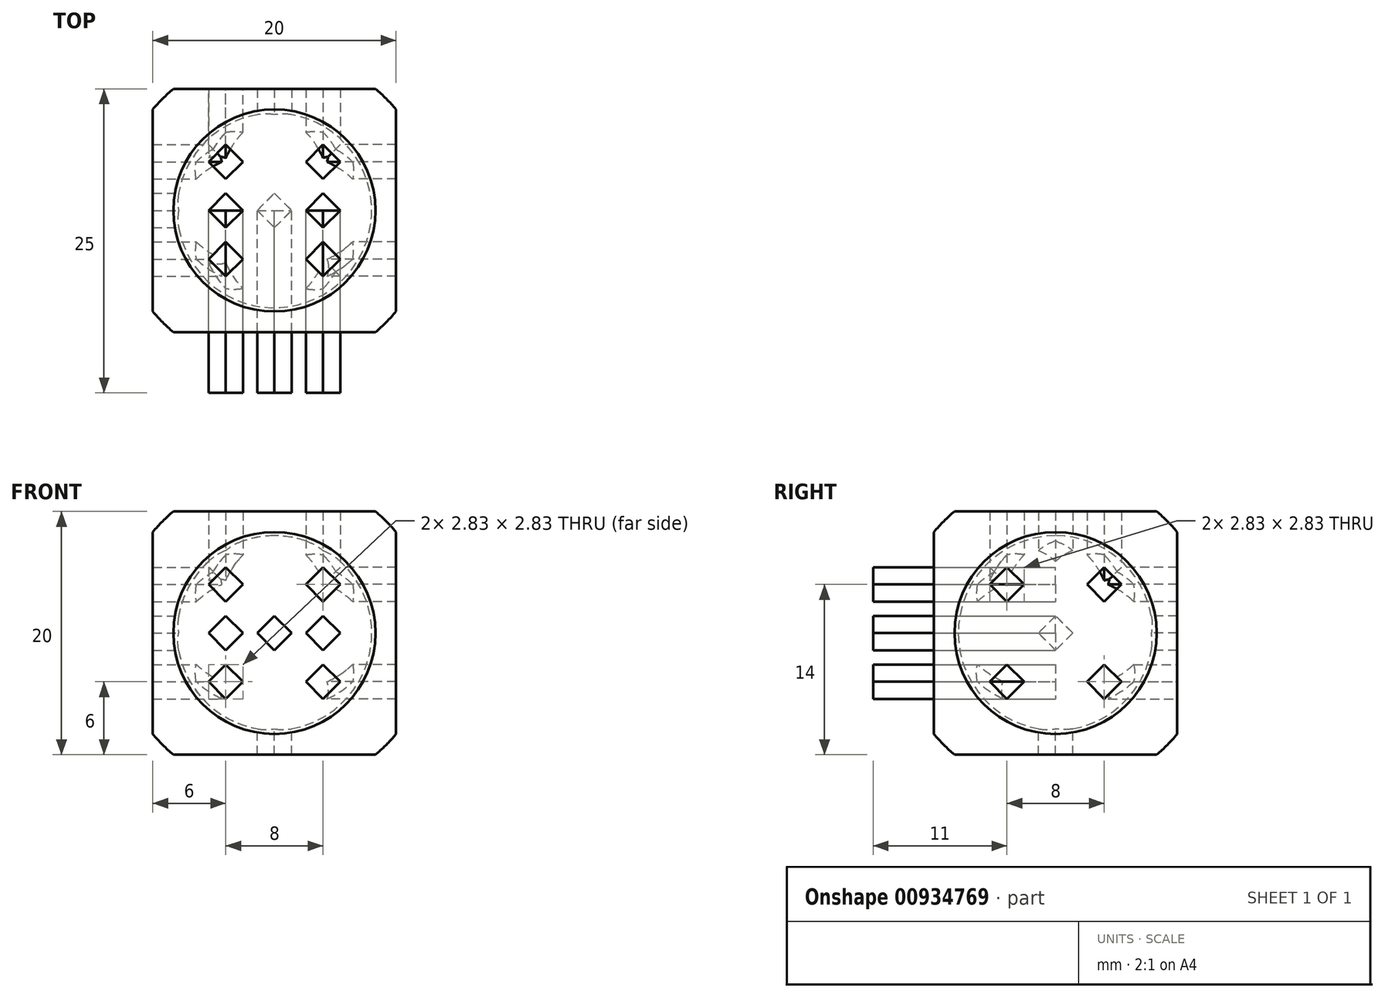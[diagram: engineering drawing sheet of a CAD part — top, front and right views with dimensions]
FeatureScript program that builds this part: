
annotation { "Feature Type Name" : "Feature", "Feature Type Description" : "" }
export const myFeature = defineFeature(function(context is Context, id is Id, definition is map)
    precondition{}
    {
        {
            var Q0;
            Q0=qCreatedBy(makeId("Front.planeOp"),FACE);
            var sketch = newSketch(context, id + "F0", { "sketchPlane" : qUnion([Q0])});
            skLineSegment(sketch, "E0.bottom", {"start": v(-10, 10) * mm, "end": v(10, 10) * mm});
            skLineSegment(sketch, "E0.top", {"start": v(-10, -10) * mm, "end": v(10, -10) * mm});
            skLineSegment(sketch, "E0.left", {"start": v(-10, 10) * mm, "end": v(-10, -10) * mm});
            skLineSegment(sketch, "E0.right", {"start": v(10, 10) * mm, "end": v(10, -10) * mm});
            skLineSegment(sketch, "E1", {"start": v(0, 0) * mm, "end": v(0, 10) * mm});
            skLineSegment(sketch, "E2", {"start": v(0, 10) * mm, "end": v(0, 0) * mm, "construction": true});
            skLineSegment(sketch, "E3", {"start": v(10, 0) * mm, "end": v(0, 0) * mm, "construction": true});
            skSolve(sketch);
        }
        {
            var Q0;
            Q0=qCreatedBy(makeId("Front.planeOp"),FACE);
            var sketch = newSketch(context, id + "F1", { "sketchPlane" : qUnion([Q0])});
            skLineSegment(sketch, "E4.bottom", {"start": v(-1, 1) * mm, "end": v(1, 1) * mm});
            skLineSegment(sketch, "E4.top", {"start": v(-1, -1) * mm, "end": v(1, -1) * mm});
            skLineSegment(sketch, "E4.left", {"start": v(-1, 1) * mm, "end": v(-1, -1) * mm});
            skLineSegment(sketch, "E4.right", {"start": v(1, 1) * mm, "end": v(1, -1) * mm});
            skSolve(sketch);
        }
        {
            var Q0;
            Q0=qCreatedBy(makeId("Right.planeOp"),FACE);
            var sketch = newSketch(context, id + "F2", { "sketchPlane" : qUnion([Q0])});
            skLineSegment(sketch, "E5", {"start": v(0, 0) * mm, "end": v(-28.1, 0) * mm, "construction": true});
            skSolve(sketch);
        }
        {
            var Q0;
            Q0 = qSketchRegion(id + "F1", true);
            extrude(context, id + "F3", {"entities" : qUnion([Q0]), "depth" : 15 * mm, "offsetDistance" : 25 * mm});
        }
        {
            var Q0;
            Q0=makeQuery(id+"F3.opExtrude","SWEPT_BODY",BODY,{"disambiguationData":[OSD([sQuery(id+"F1.wireOp",EDGE,"E4.bottom"),sQuery(id+"F1.wireOp",EDGE,"E4.top"),sQuery(id+"F1.wireOp",EDGE,"E4.left"),sQuery(id+"F1.wireOp",EDGE,"E4.right")])]});
            var Q1;
            Q1=sQuery(id+"F2.wireOp",EDGE,"E5");
            transform(context, id + "F4", {"entities" : qUnion([Q0]), "transformType" : TransformType.ROTATION, "transformAxis" : qUnion([Q1]), "angle" : 45 * degree, "makeCopy" : false});
        }
        {
            var Q0;
            Q0=makeQuery(id+"F3.opExtrude","SWEPT_BODY",BODY,{"disambiguationData":[OSD([sQuery(id+"F1.wireOp",EDGE,"E4.bottom"),sQuery(id+"F1.wireOp",EDGE,"E4.top"),sQuery(id+"F1.wireOp",EDGE,"E4.left"),sQuery(id+"F1.wireOp",EDGE,"E4.right")])]});
            transform(context, id + "F5", {"entities" : qUnion([Q0]), "transformType" : TransformType.TRANSLATION_3D, "dx" : 0 * mm, "dy" : 0 * mm, "dz" : 0 * mm, "makeCopy" : true});
        }
        {
            var Q0;
            Q0=makeQuery(id+"F5.opPattern","COPY",BODY,{"derivedFrom":makeQuery(id+"F3.opExtrude","SWEPT_BODY",BODY,{"disambiguationData":[OSD([sQuery(id+"F1.wireOp",EDGE,"E4.bottom"),sQuery(id+"F1.wireOp",EDGE,"E4.top"),sQuery(id+"F1.wireOp",EDGE,"E4.left"),sQuery(id+"F1.wireOp",EDGE,"E4.right")])]}),"instanceName":"1"});
            transform(context, id + "F6", {"entities" : qUnion([Q0]), "transformType" : TransformType.TRANSLATION_3D, "dx" : 4 * mm, "dy" : 0 * mm, "dz" : 4 * mm, "makeCopy" : false});
        }
        {
            var Q0;
            Q0=makeQuery(id+"F5.opPattern","COPY",BODY,{"derivedFrom":makeQuery(id+"F3.opExtrude","SWEPT_BODY",BODY,{"disambiguationData":[OSD([sQuery(id+"F1.wireOp",EDGE,"E4.bottom"),sQuery(id+"F1.wireOp",EDGE,"E4.top"),sQuery(id+"F1.wireOp",EDGE,"E4.left"),sQuery(id+"F1.wireOp",EDGE,"E4.right")])]}),"instanceName":"1"});
            var Q1;
            Q1=sQuery(id+"F2.wireOp",EDGE,"E5");
            transform(context, id + "F7", {"entities" : qUnion([Q0]), "transformType" : TransformType.ROTATION, "transformAxis" : qUnion([Q1]), "angle" : 90 * degree, "makeCopy" : true});
        }
        {
            var Q0;
            Q0=makeQuery(id+"F7.opPattern","COPY",BODY,{"derivedFrom":makeQuery(id+"F5.opPattern","COPY",BODY,{"derivedFrom":makeQuery(id+"F3.opExtrude","SWEPT_BODY",BODY,{"disambiguationData":[OSD([sQuery(id+"F1.wireOp",EDGE,"E4.bottom"),sQuery(id+"F1.wireOp",EDGE,"E4.top"),sQuery(id+"F1.wireOp",EDGE,"E4.left"),sQuery(id+"F1.wireOp",EDGE,"E4.right")])]}),"instanceName":"1"}),"instanceName":"1"});
            var Q1;
            Q1=makeQuery(id+"F5.opPattern","COPY",BODY,{"derivedFrom":makeQuery(id+"F3.opExtrude","SWEPT_BODY",BODY,{"disambiguationData":[OSD([sQuery(id+"F1.wireOp",EDGE,"E4.bottom"),sQuery(id+"F1.wireOp",EDGE,"E4.top"),sQuery(id+"F1.wireOp",EDGE,"E4.left"),sQuery(id+"F1.wireOp",EDGE,"E4.right")])]}),"instanceName":"1"});
            var Q2;
            Q2=qCreatedBy(makeId("Top.planeOp"),FACE);
            mirror(context, id + "F8", {"entities" : qUnion([Q0, Q1]), "mirrorPlane" : qUnion([Q2])});
        }
        {
            var Q0;
            Q0=makeQuery(id+"F3.opExtrude","SWEPT_BODY",BODY,{"disambiguationData":[OSD([sQuery(id+"F1.wireOp",EDGE,"E4.bottom"),sQuery(id+"F1.wireOp",EDGE,"E4.top"),sQuery(id+"F1.wireOp",EDGE,"E4.left"),sQuery(id+"F1.wireOp",EDGE,"E4.right")])]});
            transform(context, id + "F9", {"entities" : qUnion([Q0]), "transformType" : TransformType.TRANSLATION_3D, "dx" : 4 * mm, "dy" : 0 * mm, "dz" : 0 * mm, "makeCopy" : true});
        }
        {
            var Q0;
            Q0=makeQuery(id+"F9.opPattern","COPY",BODY,{"derivedFrom":makeQuery(id+"F3.opExtrude","SWEPT_BODY",BODY,{"disambiguationData":[OSD([sQuery(id+"F1.wireOp",EDGE,"E4.bottom"),sQuery(id+"F1.wireOp",EDGE,"E4.top"),sQuery(id+"F1.wireOp",EDGE,"E4.left"),sQuery(id+"F1.wireOp",EDGE,"E4.right")])]}),"instanceName":"1"});
            var Q1;
            Q1=sQuery(id+"F2.wireOp",EDGE,"E5");
            transform(context, id + "F10", {"entities" : qUnion([Q0]), "transformType" : TransformType.ROTATION, "transformAxis" : qUnion([Q1]), "angle" : 180 * degree, "makeCopy" : true});
        }
        {
            var Q0;
            Q0=makeQuery(id+"F3.opExtrude","SWEPT_BODY",BODY,{"disambiguationData":[OSD([sQuery(id+"F1.wireOp",EDGE,"E4.bottom"),sQuery(id+"F1.wireOp",EDGE,"E4.top"),sQuery(id+"F1.wireOp",EDGE,"E4.left"),sQuery(id+"F1.wireOp",EDGE,"E4.right")])]});
            var Q1;
            Q1=sQuery(id+"F0.wireOp",EDGE,"E3");
            transform(context, id + "F11", {"entities" : qUnion([Q0]), "transformType" : TransformType.ROTATION, "transformAxis" : qUnion([Q1]), "angle" : 90 * degree, "oppositeDirection" : true, "makeCopy" : true});
        }
        {
            var Q0;
            Q0=makeQuery(id+"F7.opPattern","COPY",BODY,{"derivedFrom":makeQuery(id+"F5.opPattern","COPY",BODY,{"derivedFrom":makeQuery(id+"F3.opExtrude","SWEPT_BODY",BODY,{"disambiguationData":[OSD([sQuery(id+"F1.wireOp",EDGE,"E4.bottom"),sQuery(id+"F1.wireOp",EDGE,"E4.top"),sQuery(id+"F1.wireOp",EDGE,"E4.left"),sQuery(id+"F1.wireOp",EDGE,"E4.right")])]}),"instanceName":"1"}),"instanceName":"1"});
            var Q1;
            Q1=makeQuery(id+"F10.opPattern","COPY",BODY,{"derivedFrom":makeQuery(id+"F9.opPattern","COPY",BODY,{"derivedFrom":makeQuery(id+"F3.opExtrude","SWEPT_BODY",BODY,{"disambiguationData":[OSD([sQuery(id+"F1.wireOp",EDGE,"E4.bottom"),sQuery(id+"F1.wireOp",EDGE,"E4.top"),sQuery(id+"F1.wireOp",EDGE,"E4.left"),sQuery(id+"F1.wireOp",EDGE,"E4.right")])]}),"instanceName":"1"}),"instanceName":"1"});
            var Q2;
            Q2=makeQuery(id+"F8.opPattern","COPY",BODY,{"derivedFrom":makeQuery(id+"F7.opPattern","COPY",BODY,{"derivedFrom":makeQuery(id+"F5.opPattern","COPY",BODY,{"derivedFrom":makeQuery(id+"F3.opExtrude","SWEPT_BODY",BODY,{"disambiguationData":[OSD([sQuery(id+"F1.wireOp",EDGE,"E4.bottom"),sQuery(id+"F1.wireOp",EDGE,"E4.top"),sQuery(id+"F1.wireOp",EDGE,"E4.left"),sQuery(id+"F1.wireOp",EDGE,"E4.right")])]}),"instanceName":"1"}),"instanceName":"1"}),"instanceName":"1"});
            var Q3;
            Q3=makeQuery(id+"F5.opPattern","COPY",BODY,{"derivedFrom":makeQuery(id+"F3.opExtrude","SWEPT_BODY",BODY,{"disambiguationData":[OSD([sQuery(id+"F1.wireOp",EDGE,"E4.bottom"),sQuery(id+"F1.wireOp",EDGE,"E4.top"),sQuery(id+"F1.wireOp",EDGE,"E4.left"),sQuery(id+"F1.wireOp",EDGE,"E4.right")])]}),"instanceName":"1"});
            var Q4;
            Q4=makeQuery(id+"F9.opPattern","COPY",BODY,{"derivedFrom":makeQuery(id+"F3.opExtrude","SWEPT_BODY",BODY,{"disambiguationData":[OSD([sQuery(id+"F1.wireOp",EDGE,"E4.bottom"),sQuery(id+"F1.wireOp",EDGE,"E4.top"),sQuery(id+"F1.wireOp",EDGE,"E4.left"),sQuery(id+"F1.wireOp",EDGE,"E4.right")])]}),"instanceName":"1"});
            var Q5;
            Q5=makeQuery(id+"F8.opPattern","COPY",BODY,{"derivedFrom":makeQuery(id+"F5.opPattern","COPY",BODY,{"derivedFrom":makeQuery(id+"F3.opExtrude","SWEPT_BODY",BODY,{"disambiguationData":[OSD([sQuery(id+"F1.wireOp",EDGE,"E4.bottom"),sQuery(id+"F1.wireOp",EDGE,"E4.top"),sQuery(id+"F1.wireOp",EDGE,"E4.left"),sQuery(id+"F1.wireOp",EDGE,"E4.right")])]}),"instanceName":"1"}),"instanceName":"1"});
            var Q6;
            Q6=sQuery(id+"F0.wireOp",EDGE,"E3");
            transform(context, id + "F12", {"entities" : qUnion([Q0, Q1, Q2, Q3, Q4, Q5]), "transformType" : TransformType.ROTATION, "transformAxis" : qUnion([Q6]), "angle" : 90 * degree, "makeCopy" : true});
        }
        {
            var Q0;
            Q0=makeQuery(id+"F7.opPattern","COPY",BODY,{"derivedFrom":makeQuery(id+"F5.opPattern","COPY",BODY,{"derivedFrom":makeQuery(id+"F3.opExtrude","SWEPT_BODY",BODY,{"disambiguationData":[OSD([sQuery(id+"F1.wireOp",EDGE,"E4.bottom"),sQuery(id+"F1.wireOp",EDGE,"E4.top"),sQuery(id+"F1.wireOp",EDGE,"E4.left"),sQuery(id+"F1.wireOp",EDGE,"E4.right")])]}),"instanceName":"1"}),"instanceName":"1"});
            var Q1;
            Q1=makeQuery(id+"F8.opPattern","COPY",BODY,{"derivedFrom":makeQuery(id+"F7.opPattern","COPY",BODY,{"derivedFrom":makeQuery(id+"F5.opPattern","COPY",BODY,{"derivedFrom":makeQuery(id+"F3.opExtrude","SWEPT_BODY",BODY,{"disambiguationData":[OSD([sQuery(id+"F1.wireOp",EDGE,"E4.bottom"),sQuery(id+"F1.wireOp",EDGE,"E4.top"),sQuery(id+"F1.wireOp",EDGE,"E4.left"),sQuery(id+"F1.wireOp",EDGE,"E4.right")])]}),"instanceName":"1"}),"instanceName":"1"}),"instanceName":"1"});
            var Q2;
            Q2=makeQuery(id+"F8.opPattern","COPY",BODY,{"derivedFrom":makeQuery(id+"F5.opPattern","COPY",BODY,{"derivedFrom":makeQuery(id+"F3.opExtrude","SWEPT_BODY",BODY,{"disambiguationData":[OSD([sQuery(id+"F1.wireOp",EDGE,"E4.bottom"),sQuery(id+"F1.wireOp",EDGE,"E4.top"),sQuery(id+"F1.wireOp",EDGE,"E4.left"),sQuery(id+"F1.wireOp",EDGE,"E4.right")])]}),"instanceName":"1"}),"instanceName":"1"});
            var Q3;
            Q3=makeQuery(id+"F5.opPattern","COPY",BODY,{"derivedFrom":makeQuery(id+"F3.opExtrude","SWEPT_BODY",BODY,{"disambiguationData":[OSD([sQuery(id+"F1.wireOp",EDGE,"E4.bottom"),sQuery(id+"F1.wireOp",EDGE,"E4.top"),sQuery(id+"F1.wireOp",EDGE,"E4.left"),sQuery(id+"F1.wireOp",EDGE,"E4.right")])]}),"instanceName":"1"});
            var Q4;
            Q4=makeQuery(id+"F3.opExtrude","SWEPT_BODY",BODY,{"disambiguationData":[OSD([sQuery(id+"F1.wireOp",EDGE,"E4.bottom"),sQuery(id+"F1.wireOp",EDGE,"E4.top"),sQuery(id+"F1.wireOp",EDGE,"E4.left"),sQuery(id+"F1.wireOp",EDGE,"E4.right")])]});
            var Q5;
            Q5=sQuery(id+"F0.wireOp",EDGE,"E1");
            transform(context, id + "F13", {"entities" : qUnion([Q0, Q1, Q2, Q3, Q4]), "transformType" : TransformType.ROTATION, "transformAxis" : qUnion([Q5]), "angle" : 180 * degree, "makeCopy" : true});
        }
        {
            var Q0;
            Q0=makeQuery(id+"F7.opPattern","COPY",BODY,{"derivedFrom":makeQuery(id+"F5.opPattern","COPY",BODY,{"derivedFrom":makeQuery(id+"F3.opExtrude","SWEPT_BODY",BODY,{"disambiguationData":[OSD([sQuery(id+"F1.wireOp",EDGE,"E4.bottom"),sQuery(id+"F1.wireOp",EDGE,"E4.top"),sQuery(id+"F1.wireOp",EDGE,"E4.left"),sQuery(id+"F1.wireOp",EDGE,"E4.right")])]}),"instanceName":"1"}),"instanceName":"1"});
            var Q1;
            Q1=makeQuery(id+"F8.opPattern","COPY",BODY,{"derivedFrom":makeQuery(id+"F5.opPattern","COPY",BODY,{"derivedFrom":makeQuery(id+"F3.opExtrude","SWEPT_BODY",BODY,{"disambiguationData":[OSD([sQuery(id+"F1.wireOp",EDGE,"E4.bottom"),sQuery(id+"F1.wireOp",EDGE,"E4.top"),sQuery(id+"F1.wireOp",EDGE,"E4.left"),sQuery(id+"F1.wireOp",EDGE,"E4.right")])]}),"instanceName":"1"}),"instanceName":"1"});
            var Q2;
            Q2=makeQuery(id+"F5.opPattern","COPY",BODY,{"derivedFrom":makeQuery(id+"F3.opExtrude","SWEPT_BODY",BODY,{"disambiguationData":[OSD([sQuery(id+"F1.wireOp",EDGE,"E4.bottom"),sQuery(id+"F1.wireOp",EDGE,"E4.top"),sQuery(id+"F1.wireOp",EDGE,"E4.left"),sQuery(id+"F1.wireOp",EDGE,"E4.right")])]}),"instanceName":"1"});
            var Q3;
            Q3=makeQuery(id+"F8.opPattern","COPY",BODY,{"derivedFrom":makeQuery(id+"F7.opPattern","COPY",BODY,{"derivedFrom":makeQuery(id+"F5.opPattern","COPY",BODY,{"derivedFrom":makeQuery(id+"F3.opExtrude","SWEPT_BODY",BODY,{"disambiguationData":[OSD([sQuery(id+"F1.wireOp",EDGE,"E4.bottom"),sQuery(id+"F1.wireOp",EDGE,"E4.top"),sQuery(id+"F1.wireOp",EDGE,"E4.left"),sQuery(id+"F1.wireOp",EDGE,"E4.right")])]}),"instanceName":"1"}),"instanceName":"1"}),"instanceName":"1"});
            var Q4;
            Q4=sQuery(id+"F0.wireOp",EDGE,"E2");
            transform(context, id + "F14", {"entities" : qUnion([Q0, Q1, Q2, Q3]), "transformType" : TransformType.ROTATION, "transformAxis" : qUnion([Q4]), "angle" : 90 * degree, "oppositeDirection" : true, "makeCopy" : true});
        }
        {
            var Q0;
            Q0=makeQuery(id+"F8.opPattern","COPY",BODY,{"derivedFrom":makeQuery(id+"F7.opPattern","COPY",BODY,{"derivedFrom":makeQuery(id+"F5.opPattern","COPY",BODY,{"derivedFrom":makeQuery(id+"F3.opExtrude","SWEPT_BODY",BODY,{"disambiguationData":[OSD([sQuery(id+"F1.wireOp",EDGE,"E4.bottom"),sQuery(id+"F1.wireOp",EDGE,"E4.top"),sQuery(id+"F1.wireOp",EDGE,"E4.left"),sQuery(id+"F1.wireOp",EDGE,"E4.right")])]}),"instanceName":"1"}),"instanceName":"1"}),"instanceName":"1"});
            var Q1;
            Q1=makeQuery(id+"F3.opExtrude","SWEPT_BODY",BODY,{"disambiguationData":[OSD([sQuery(id+"F1.wireOp",EDGE,"E4.bottom"),sQuery(id+"F1.wireOp",EDGE,"E4.top"),sQuery(id+"F1.wireOp",EDGE,"E4.left"),sQuery(id+"F1.wireOp",EDGE,"E4.right")])]});
            var Q2;
            Q2=makeQuery(id+"F5.opPattern","COPY",BODY,{"derivedFrom":makeQuery(id+"F3.opExtrude","SWEPT_BODY",BODY,{"disambiguationData":[OSD([sQuery(id+"F1.wireOp",EDGE,"E4.bottom"),sQuery(id+"F1.wireOp",EDGE,"E4.top"),sQuery(id+"F1.wireOp",EDGE,"E4.left"),sQuery(id+"F1.wireOp",EDGE,"E4.right")])]}),"instanceName":"1"});
            var Q3;
            Q3=sQuery(id+"F0.wireOp",EDGE,"E2");
            transform(context, id + "F15", {"entities" : qUnion([Q0, Q1, Q2]), "transformType" : TransformType.ROTATION, "transformAxis" : qUnion([Q3]), "angle" : 90 * degree, "makeCopy" : true});
        }
        {
            var Q0;
            Q0=makeQuery(id+"F8.opPattern","COPY",BODY,{"derivedFrom":makeQuery(id+"F7.opPattern","COPY",BODY,{"derivedFrom":makeQuery(id+"F5.opPattern","COPY",BODY,{"derivedFrom":makeQuery(id+"F3.opExtrude","SWEPT_BODY",BODY,{"disambiguationData":[OSD([sQuery(id+"F1.wireOp",EDGE,"E4.bottom"),sQuery(id+"F1.wireOp",EDGE,"E4.top"),sQuery(id+"F1.wireOp",EDGE,"E4.left"),sQuery(id+"F1.wireOp",EDGE,"E4.right")])]}),"instanceName":"1"}),"instanceName":"1"}),"instanceName":"1"});
            var Q1;
            Q1=makeQuery(id+"F5.opPattern","COPY",BODY,{"derivedFrom":makeQuery(id+"F3.opExtrude","SWEPT_BODY",BODY,{"disambiguationData":[OSD([sQuery(id+"F1.wireOp",EDGE,"E4.bottom"),sQuery(id+"F1.wireOp",EDGE,"E4.top"),sQuery(id+"F1.wireOp",EDGE,"E4.left"),sQuery(id+"F1.wireOp",EDGE,"E4.right")])]}),"instanceName":"1"});
            transform(context, id + "F16", {"entities" : qUnion([Q0, Q1]), "transformType" : TransformType.TRANSLATION_3D, "dx" : 0 * mm, "dy" : 0 * mm, "dz" : 0 * mm, "makeCopy" : true});
        }
        {
            var Q0;
            Q0=qCreatedBy(makeId("Front.planeOp"),FACE);
            var sketch = newSketch(context, id + "F17", { "sketchPlane" : qUnion([Q0])});
            skArc(sketch, "E6", {"start": v(0, -13) * mm, "mid": v(13, 0) * mm, "end": v(0, 13) * mm});
            skArc(sketch, "E7", {"start": v(0, -8) * mm, "mid": v(8, 0) * mm, "end": v(0, 8) * mm});
            skLineSegment(sketch, "E8", {"start": v(0, 13) * mm, "end": v(0, 8) * mm});
            skLineSegment(sketch, "E9", {"start": v(0, -8) * mm, "end": v(0, -13) * mm});
            skSolve(sketch);
        }
        {
            var Q0;
            Q0 = qSketchRegion(id + "F0", true);
            extrude(context, id + "F18", {"entities" : qUnion([Q0]), "endBound" : BoundingType.SYMMETRIC, "depth" : 20 * mm, "offsetDistance" : 25 * mm});
        }
        {
            var Q0;
            Q0 = qSketchRegion(id + "F17", true);
            var Q1;
            Q1=sQuery(id+"F0.wireOp",EDGE,"E1");
            revolve(context, id + "F19", {"surfaceOperationType" : NewSurfaceOperationType.NEW, "entities" : qUnion([Q0]), "axis" : qUnion([Q1]), "revolveType" : RevolveType.FULL});
        }
        {
            var Q0;
            Q0=makeQuery(id+"F18.opExtrude","SWEPT_BODY",BODY,{"disambiguationData":[OSD([sQuery(id+"F0.wireOp",EDGE,"E0.bottom"),sQuery(id+"F0.wireOp",EDGE,"E0.top"),sQuery(id+"F0.wireOp",EDGE,"E0.left"),sQuery(id+"F0.wireOp",EDGE,"E0.right")])]});
            var Q1;
            Q1=makeQuery(id+"F19.opRevolve","SWEPT_BODY",BODY,{"disambiguationData":[OSD([sQuery(id+"F17.wireOp",EDGE,"E6"),sQuery(id+"F17.wireOp",EDGE,"E7"),sQuery(id+"F17.wireOp",EDGE,"E8"),sQuery(id+"F17.wireOp",EDGE,"E9")])]});
            booleanBodies(context, id + "F20", {"operationType" : BooleanOperationType.INTERSECTION, "tools" : qUnion([Q0, Q1])});
        }
        {
            var Q0;
            Q0=makeQuery(id+"F16.opPattern","COPY",BODY,{"derivedFrom":makeQuery(id+"F5.opPattern","COPY",BODY,{"derivedFrom":makeQuery(id+"F3.opExtrude","SWEPT_BODY",BODY,{"disambiguationData":[OSD([sQuery(id+"F1.wireOp",EDGE,"E4.bottom"),sQuery(id+"F1.wireOp",EDGE,"E4.top"),sQuery(id+"F1.wireOp",EDGE,"E4.left"),sQuery(id+"F1.wireOp",EDGE,"E4.right")])]}),"instanceName":"1"}),"instanceName":"1"});
            var Q1;
            Q1=makeQuery(id+"F16.opPattern","COPY",BODY,{"derivedFrom":makeQuery(id+"F8.opPattern","COPY",BODY,{"derivedFrom":makeQuery(id+"F7.opPattern","COPY",BODY,{"derivedFrom":makeQuery(id+"F5.opPattern","COPY",BODY,{"derivedFrom":makeQuery(id+"F3.opExtrude","SWEPT_BODY",BODY,{"disambiguationData":[OSD([sQuery(id+"F1.wireOp",EDGE,"E4.bottom"),sQuery(id+"F1.wireOp",EDGE,"E4.top"),sQuery(id+"F1.wireOp",EDGE,"E4.left"),sQuery(id+"F1.wireOp",EDGE,"E4.right")])]}),"instanceName":"1"}),"instanceName":"1"}),"instanceName":"1"}),"instanceName":"1"});
            var Q2;
            Q2=makeQuery(id+"F14.opPattern","COPY",BODY,{"derivedFrom":makeQuery(id+"F8.opPattern","COPY",BODY,{"derivedFrom":makeQuery(id+"F7.opPattern","COPY",BODY,{"derivedFrom":makeQuery(id+"F5.opPattern","COPY",BODY,{"derivedFrom":makeQuery(id+"F3.opExtrude","SWEPT_BODY",BODY,{"disambiguationData":[OSD([sQuery(id+"F1.wireOp",EDGE,"E4.bottom"),sQuery(id+"F1.wireOp",EDGE,"E4.top"),sQuery(id+"F1.wireOp",EDGE,"E4.left"),sQuery(id+"F1.wireOp",EDGE,"E4.right")])]}),"instanceName":"1"}),"instanceName":"1"}),"instanceName":"1"}),"instanceName":"1"});
            var Q3;
            Q3=makeQuery(id+"F14.opPattern","COPY",BODY,{"derivedFrom":makeQuery(id+"F7.opPattern","COPY",BODY,{"derivedFrom":makeQuery(id+"F5.opPattern","COPY",BODY,{"derivedFrom":makeQuery(id+"F3.opExtrude","SWEPT_BODY",BODY,{"disambiguationData":[OSD([sQuery(id+"F1.wireOp",EDGE,"E4.bottom"),sQuery(id+"F1.wireOp",EDGE,"E4.top"),sQuery(id+"F1.wireOp",EDGE,"E4.left"),sQuery(id+"F1.wireOp",EDGE,"E4.right")])]}),"instanceName":"1"}),"instanceName":"1"}),"instanceName":"1"});
            var Q4;
            Q4=makeQuery(id+"F14.opPattern","COPY",BODY,{"derivedFrom":makeQuery(id+"F5.opPattern","COPY",BODY,{"derivedFrom":makeQuery(id+"F3.opExtrude","SWEPT_BODY",BODY,{"disambiguationData":[OSD([sQuery(id+"F1.wireOp",EDGE,"E4.bottom"),sQuery(id+"F1.wireOp",EDGE,"E4.top"),sQuery(id+"F1.wireOp",EDGE,"E4.left"),sQuery(id+"F1.wireOp",EDGE,"E4.right")])]}),"instanceName":"1"}),"instanceName":"1"});
            var Q5;
            Q5=makeQuery(id+"F14.opPattern","COPY",BODY,{"derivedFrom":makeQuery(id+"F8.opPattern","COPY",BODY,{"derivedFrom":makeQuery(id+"F5.opPattern","COPY",BODY,{"derivedFrom":makeQuery(id+"F3.opExtrude","SWEPT_BODY",BODY,{"disambiguationData":[OSD([sQuery(id+"F1.wireOp",EDGE,"E4.bottom"),sQuery(id+"F1.wireOp",EDGE,"E4.top"),sQuery(id+"F1.wireOp",EDGE,"E4.left"),sQuery(id+"F1.wireOp",EDGE,"E4.right")])]}),"instanceName":"1"}),"instanceName":"1"}),"instanceName":"1"});
            var Q6;
            Q6=makeQuery(id+"F12.opPattern","COPY",BODY,{"derivedFrom":makeQuery(id+"F8.opPattern","COPY",BODY,{"derivedFrom":makeQuery(id+"F5.opPattern","COPY",BODY,{"derivedFrom":makeQuery(id+"F3.opExtrude","SWEPT_BODY",BODY,{"disambiguationData":[OSD([sQuery(id+"F1.wireOp",EDGE,"E4.bottom"),sQuery(id+"F1.wireOp",EDGE,"E4.top"),sQuery(id+"F1.wireOp",EDGE,"E4.left"),sQuery(id+"F1.wireOp",EDGE,"E4.right")])]}),"instanceName":"1"}),"instanceName":"1"}),"instanceName":"1"});
            var Q7;
            Q7=makeQuery(id+"F12.opPattern","COPY",BODY,{"derivedFrom":makeQuery(id+"F9.opPattern","COPY",BODY,{"derivedFrom":makeQuery(id+"F3.opExtrude","SWEPT_BODY",BODY,{"disambiguationData":[OSD([sQuery(id+"F1.wireOp",EDGE,"E4.bottom"),sQuery(id+"F1.wireOp",EDGE,"E4.top"),sQuery(id+"F1.wireOp",EDGE,"E4.left"),sQuery(id+"F1.wireOp",EDGE,"E4.right")])]}),"instanceName":"1"}),"instanceName":"1"});
            var Q8;
            Q8=makeQuery(id+"F13.opPattern","COPY",BODY,{"derivedFrom":makeQuery(id+"F5.opPattern","COPY",BODY,{"derivedFrom":makeQuery(id+"F3.opExtrude","SWEPT_BODY",BODY,{"disambiguationData":[OSD([sQuery(id+"F1.wireOp",EDGE,"E4.bottom"),sQuery(id+"F1.wireOp",EDGE,"E4.top"),sQuery(id+"F1.wireOp",EDGE,"E4.left"),sQuery(id+"F1.wireOp",EDGE,"E4.right")])]}),"instanceName":"1"}),"instanceName":"1"});
            var Q9;
            Q9=makeQuery(id+"F12.opPattern","COPY",BODY,{"derivedFrom":makeQuery(id+"F5.opPattern","COPY",BODY,{"derivedFrom":makeQuery(id+"F3.opExtrude","SWEPT_BODY",BODY,{"disambiguationData":[OSD([sQuery(id+"F1.wireOp",EDGE,"E4.bottom"),sQuery(id+"F1.wireOp",EDGE,"E4.top"),sQuery(id+"F1.wireOp",EDGE,"E4.left"),sQuery(id+"F1.wireOp",EDGE,"E4.right")])]}),"instanceName":"1"}),"instanceName":"1"});
            var Q10;
            Q10=makeQuery(id+"F12.opPattern","COPY",BODY,{"derivedFrom":makeQuery(id+"F7.opPattern","COPY",BODY,{"derivedFrom":makeQuery(id+"F5.opPattern","COPY",BODY,{"derivedFrom":makeQuery(id+"F3.opExtrude","SWEPT_BODY",BODY,{"disambiguationData":[OSD([sQuery(id+"F1.wireOp",EDGE,"E4.bottom"),sQuery(id+"F1.wireOp",EDGE,"E4.top"),sQuery(id+"F1.wireOp",EDGE,"E4.left"),sQuery(id+"F1.wireOp",EDGE,"E4.right")])]}),"instanceName":"1"}),"instanceName":"1"}),"instanceName":"1"});
            var Q11;
            Q11=makeQuery(id+"F12.opPattern","COPY",BODY,{"derivedFrom":makeQuery(id+"F10.opPattern","COPY",BODY,{"derivedFrom":makeQuery(id+"F9.opPattern","COPY",BODY,{"derivedFrom":makeQuery(id+"F3.opExtrude","SWEPT_BODY",BODY,{"disambiguationData":[OSD([sQuery(id+"F1.wireOp",EDGE,"E4.bottom"),sQuery(id+"F1.wireOp",EDGE,"E4.top"),sQuery(id+"F1.wireOp",EDGE,"E4.left"),sQuery(id+"F1.wireOp",EDGE,"E4.right")])]}),"instanceName":"1"}),"instanceName":"1"}),"instanceName":"1"});
            var Q12;
            Q12=makeQuery(id+"F12.opPattern","COPY",BODY,{"derivedFrom":makeQuery(id+"F8.opPattern","COPY",BODY,{"derivedFrom":makeQuery(id+"F7.opPattern","COPY",BODY,{"derivedFrom":makeQuery(id+"F5.opPattern","COPY",BODY,{"derivedFrom":makeQuery(id+"F3.opExtrude","SWEPT_BODY",BODY,{"disambiguationData":[OSD([sQuery(id+"F1.wireOp",EDGE,"E4.bottom"),sQuery(id+"F1.wireOp",EDGE,"E4.top"),sQuery(id+"F1.wireOp",EDGE,"E4.left"),sQuery(id+"F1.wireOp",EDGE,"E4.right")])]}),"instanceName":"1"}),"instanceName":"1"}),"instanceName":"1"}),"instanceName":"1"});
            var Q13;
            Q13=makeQuery(id+"F13.opPattern","COPY",BODY,{"derivedFrom":makeQuery(id+"F7.opPattern","COPY",BODY,{"derivedFrom":makeQuery(id+"F5.opPattern","COPY",BODY,{"derivedFrom":makeQuery(id+"F3.opExtrude","SWEPT_BODY",BODY,{"disambiguationData":[OSD([sQuery(id+"F1.wireOp",EDGE,"E4.bottom"),sQuery(id+"F1.wireOp",EDGE,"E4.top"),sQuery(id+"F1.wireOp",EDGE,"E4.left"),sQuery(id+"F1.wireOp",EDGE,"E4.right")])]}),"instanceName":"1"}),"instanceName":"1"}),"instanceName":"1"});
            var Q14;
            Q14=makeQuery(id+"F13.opPattern","COPY",BODY,{"derivedFrom":makeQuery(id+"F8.opPattern","COPY",BODY,{"derivedFrom":makeQuery(id+"F7.opPattern","COPY",BODY,{"derivedFrom":makeQuery(id+"F5.opPattern","COPY",BODY,{"derivedFrom":makeQuery(id+"F3.opExtrude","SWEPT_BODY",BODY,{"disambiguationData":[OSD([sQuery(id+"F1.wireOp",EDGE,"E4.bottom"),sQuery(id+"F1.wireOp",EDGE,"E4.top"),sQuery(id+"F1.wireOp",EDGE,"E4.left"),sQuery(id+"F1.wireOp",EDGE,"E4.right")])]}),"instanceName":"1"}),"instanceName":"1"}),"instanceName":"1"}),"instanceName":"1"});
            var Q15;
            Q15=makeQuery(id+"F13.opPattern","COPY",BODY,{"derivedFrom":makeQuery(id+"F8.opPattern","COPY",BODY,{"derivedFrom":makeQuery(id+"F5.opPattern","COPY",BODY,{"derivedFrom":makeQuery(id+"F3.opExtrude","SWEPT_BODY",BODY,{"disambiguationData":[OSD([sQuery(id+"F1.wireOp",EDGE,"E4.bottom"),sQuery(id+"F1.wireOp",EDGE,"E4.top"),sQuery(id+"F1.wireOp",EDGE,"E4.left"),sQuery(id+"F1.wireOp",EDGE,"E4.right")])]}),"instanceName":"1"}),"instanceName":"1"}),"instanceName":"1"});
            var Q16;
            Q16=makeQuery(id+"F13.opPattern","COPY",BODY,{"derivedFrom":makeQuery(id+"F3.opExtrude","SWEPT_BODY",BODY,{"disambiguationData":[OSD([sQuery(id+"F1.wireOp",EDGE,"E4.bottom"),sQuery(id+"F1.wireOp",EDGE,"E4.top"),sQuery(id+"F1.wireOp",EDGE,"E4.left"),sQuery(id+"F1.wireOp",EDGE,"E4.right")])]}),"instanceName":"1"});
            var Q17;
            Q17=makeQuery(id+"F11.opPattern","COPY",BODY,{"derivedFrom":makeQuery(id+"F3.opExtrude","SWEPT_BODY",BODY,{"disambiguationData":[OSD([sQuery(id+"F1.wireOp",EDGE,"E4.bottom"),sQuery(id+"F1.wireOp",EDGE,"E4.top"),sQuery(id+"F1.wireOp",EDGE,"E4.left"),sQuery(id+"F1.wireOp",EDGE,"E4.right")])]}),"instanceName":"1"});
            var Q18;
            Q18=makeQuery(id+"F15.opPattern","COPY",BODY,{"derivedFrom":makeQuery(id+"F3.opExtrude","SWEPT_BODY",BODY,{"disambiguationData":[OSD([sQuery(id+"F1.wireOp",EDGE,"E4.bottom"),sQuery(id+"F1.wireOp",EDGE,"E4.top"),sQuery(id+"F1.wireOp",EDGE,"E4.left"),sQuery(id+"F1.wireOp",EDGE,"E4.right")])]}),"instanceName":"1"});
            var Q19;
            Q19=makeQuery(id+"F15.opPattern","COPY",BODY,{"derivedFrom":makeQuery(id+"F8.opPattern","COPY",BODY,{"derivedFrom":makeQuery(id+"F7.opPattern","COPY",BODY,{"derivedFrom":makeQuery(id+"F5.opPattern","COPY",BODY,{"derivedFrom":makeQuery(id+"F3.opExtrude","SWEPT_BODY",BODY,{"disambiguationData":[OSD([sQuery(id+"F1.wireOp",EDGE,"E4.bottom"),sQuery(id+"F1.wireOp",EDGE,"E4.top"),sQuery(id+"F1.wireOp",EDGE,"E4.left"),sQuery(id+"F1.wireOp",EDGE,"E4.right")])]}),"instanceName":"1"}),"instanceName":"1"}),"instanceName":"1"}),"instanceName":"1"});
            var Q20;
            Q20=makeQuery(id+"F15.opPattern","COPY",BODY,{"derivedFrom":makeQuery(id+"F5.opPattern","COPY",BODY,{"derivedFrom":makeQuery(id+"F3.opExtrude","SWEPT_BODY",BODY,{"disambiguationData":[OSD([sQuery(id+"F1.wireOp",EDGE,"E4.bottom"),sQuery(id+"F1.wireOp",EDGE,"E4.top"),sQuery(id+"F1.wireOp",EDGE,"E4.left"),sQuery(id+"F1.wireOp",EDGE,"E4.right")])]}),"instanceName":"1"}),"instanceName":"1"});
            var Q21;
            Q21=makeQuery(id+"F20.opBoolean","INTERSECT",BODY,{"derivedFrom":[makeQuery(id+"F18.opExtrude","SWEPT_BODY",BODY,{"disambiguationData":[OSD([sQuery(id+"F0.wireOp",EDGE,"E0.bottom"),sQuery(id+"F0.wireOp",EDGE,"E0.top"),sQuery(id+"F0.wireOp",EDGE,"E0.left"),sQuery(id+"F0.wireOp",EDGE,"E0.right")])]}),makeQuery(id+"F19.opRevolve","SWEPT_BODY",BODY,{"disambiguationData":[OSD([sQuery(id+"F17.wireOp",EDGE,"E6"),sQuery(id+"F17.wireOp",EDGE,"E7"),sQuery(id+"F17.wireOp",EDGE,"E8"),sQuery(id+"F17.wireOp",EDGE,"E9")])]})]});
            booleanBodies(context, id + "F21", {"operationType" : BooleanOperationType.SUBTRACTION, "tools" : qUnion([Q0, Q1, Q2, Q3, Q4, Q5, Q6, Q7, Q8, Q9, Q10, Q11, Q12, Q13, Q14, Q15, Q16, Q17, Q18, Q19, Q20]), "targets" : qUnion([Q21])});
        }
    });
